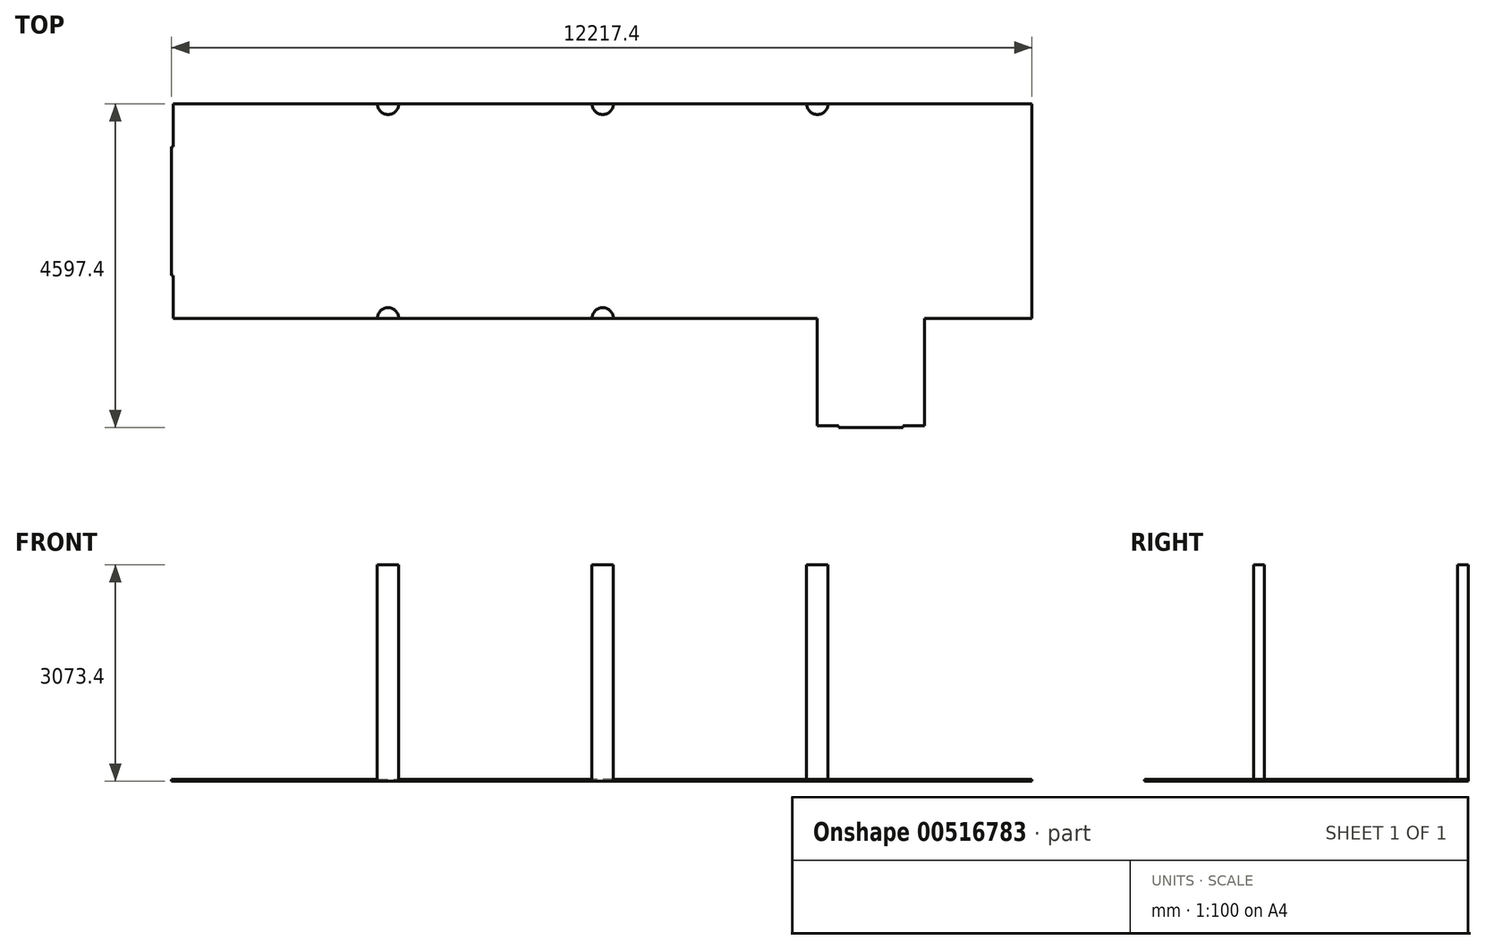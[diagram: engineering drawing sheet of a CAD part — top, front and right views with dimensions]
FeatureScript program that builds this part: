
annotation { "Feature Type Name" : "Feature", "Feature Type Description" : "" }
export const myFeature = defineFeature(function(context is Context, id is Id, definition is map)
    precondition{}
    {
        {
            var Q0;
            Q0=qCreatedBy(makeId("Top.planeOp"),FACE);
            var sketch = newSketch(context, id + "F0", { "sketchPlane" : qUnion([Q0])});
            skLineSegment(sketch, "E0.bottom", {"start": v(0, 0) * mm, "end": v(12192, 0) * mm});
            skLineSegment(sketch, "E0.top", {"start": v(0, -3048) * mm, "end": v(9144, -3048) * mm});
            skLineSegment(sketch, "E0.left", {"start": v(0, 0) * mm, "end": v(0, -3048) * mm});
            skLineSegment(sketch, "E0.right", {"start": v(12192, 0) * mm, "end": v(12192, -3048) * mm});
            skLineSegment(sketch, "E1.top", {"start": v(10668, -4572) * mm, "end": v(9144, -4572) * mm});
            skLineSegment(sketch, "E1.left", {"start": v(10668, -3048) * mm, "end": v(10668, -4572) * mm});
            skLineSegment(sketch, "E1.right", {"start": v(9144, -3048) * mm, "end": v(9144, -4572) * mm});
            skArc(sketch, "E2", {"start": v(3200.4, -3048) * mm, "mid": v(3048, -2895.6) * mm, "end": v(2895.6, -3048) * mm});
            skArc(sketch, "E3", {"start": v(6248.4, -3048) * mm, "mid": v(6096, -2895.6) * mm, "end": v(5943.6, -3048) * mm});
            skArc(sketch, "E4", {"start": v(5943.6, 0) * mm, "mid": v(6096, -152.4) * mm, "end": v(6248.4, 0) * mm});
            skArc(sketch, "E5", {"start": v(2895.6, 0) * mm, "mid": v(3048, -152.4) * mm, "end": v(3200.4, 0) * mm});
            skArc(sketch, "E6", {"start": v(8991.6, 0) * mm, "mid": v(9144, -152.4) * mm, "end": v(9296.4, 0) * mm});
            skLineSegment(sketch, "E7.trimOffspring", {"start": v(10668, -3048) * mm, "end": v(12192, -3048) * mm});
            skSolve(sketch);
        }
        {
            var Q0;
            Q0 = qSketchRegion(id + "F0", true);
            extrude(context, id + "F1", {"entities" : qUnion([Q0]), "depth" : -25.4 * mm, "offsetDistance" : 25.4 * mm});
        }
        {
            var Q0;
            {var subQ0=sQuery(id+"F0.wireOp",EDGE,"E5");Q0=makeQuery(id+"F0.imprint","IMPRINT",FACE,{"disambiguationData":[TD([[makeQuery(id+"F0.imprint","IMPRINT",EDGE,{"derivedFrom":subQ0}),1.0]])]});}
            var Q1;
            {var subQ0=sQuery(id+"F0.wireOp",EDGE,"E4");Q1=makeQuery(id+"F0.imprint","IMPRINT",FACE,{"disambiguationData":[TD([[makeQuery(id+"F0.imprint","IMPRINT",EDGE,{"derivedFrom":subQ0}),1.0]])]});}
            var Q2;
            {var subQ0=sQuery(id+"F0.wireOp",EDGE,"E2");Q2=makeQuery(id+"F0.imprint","IMPRINT",FACE,{"disambiguationData":[TD([[makeQuery(id+"F0.imprint","IMPRINT",EDGE,{"derivedFrom":subQ0}),1.0]])]});}
            var Q3;
            {var subQ0=sQuery(id+"F0.wireOp",EDGE,"E3");Q3=makeQuery(id+"F0.imprint","IMPRINT",FACE,{"disambiguationData":[TD([[makeQuery(id+"F0.imprint","IMPRINT",EDGE,{"derivedFrom":subQ0}),1.0]])]});}
            var Q4;
            {var subQ0=sQuery(id+"F0.wireOp",EDGE,"E6");Q4=makeQuery(id+"F0.imprint","IMPRINT",FACE,{"disambiguationData":[TD([[makeQuery(id+"F0.imprint","IMPRINT",EDGE,{"derivedFrom":subQ0}),1.0]])]});}
            extrude(context, id + "F2", {"entities" : qUnion([Q0, Q1, Q2, Q3, Q4]), "operationType" : NewBodyOperationType.ADD, "depth" : 3048 * mm, "offsetDistance" : 25.4 * mm});
        }
        {
            var Q0;
            Q0=makeQuery(id+"F1.opExtrude","SWEPT_FACE",FACE,{"disambiguationData":[OSD([sQuery(id+"F0.wireOp",EDGE,"E1.top")])]});
            var sketch = newSketch(context, id + "F3", { "sketchPlane" : qUnion([Q0])});
            skLineSegment(sketch, "E8.bottom", {"start": v(10363.2, -25.4) * mm, "end": v(9448.8, -25.4) * mm});
            skLineSegment(sketch, "E8.top", {"start": v(10363.2, 0) * mm, "end": v(9448.8, 0) * mm});
            skLineSegment(sketch, "E8.left", {"start": v(10363.2, -25.4) * mm, "end": v(10363.2, 0) * mm});
            skLineSegment(sketch, "E8.right", {"start": v(9448.8, -25.4) * mm, "end": v(9448.8, 0) * mm});
            skSolve(sketch);
        }
        {
            var Q0;
            Q0 = qSketchRegion(id + "F3", true);
            extrude(context, id + "F4", {"entities" : qUnion([Q0]), "operationType" : NewBodyOperationType.ADD, "depth" : 25.4 * mm, "offsetDistance" : 25.4 * mm});
        }
        {
            var Q0;
            Q0=makeQuery(id+"F1.opExtrude","SWEPT_FACE",FACE,{"disambiguationData":[OSD([sQuery(id+"F0.wireOp",EDGE,"E0.left")])]});
            var sketch = newSketch(context, id + "F5", { "sketchPlane" : qUnion([Q0])});
            skLineSegment(sketch, "E9.bottom", {"start": v(2438.4, -25.4) * mm, "end": v(609.6, -25.4) * mm});
            skLineSegment(sketch, "E9.top", {"start": v(2438.4, 0) * mm, "end": v(609.6, 0) * mm});
            skLineSegment(sketch, "E9.left", {"start": v(2438.4, -25.4) * mm, "end": v(2438.4, 0) * mm});
            skLineSegment(sketch, "E9.right", {"start": v(609.6, -25.4) * mm, "end": v(609.6, 0) * mm});
            skSolve(sketch);
        }
        {
            var Q0;
            Q0 = qSketchRegion(id + "F5", true);
            extrude(context, id + "F6", {"entities" : qUnion([Q0]), "operationType" : NewBodyOperationType.ADD, "depth" : 25.4 * mm, "offsetDistance" : 25.4 * mm});
        }
    });
